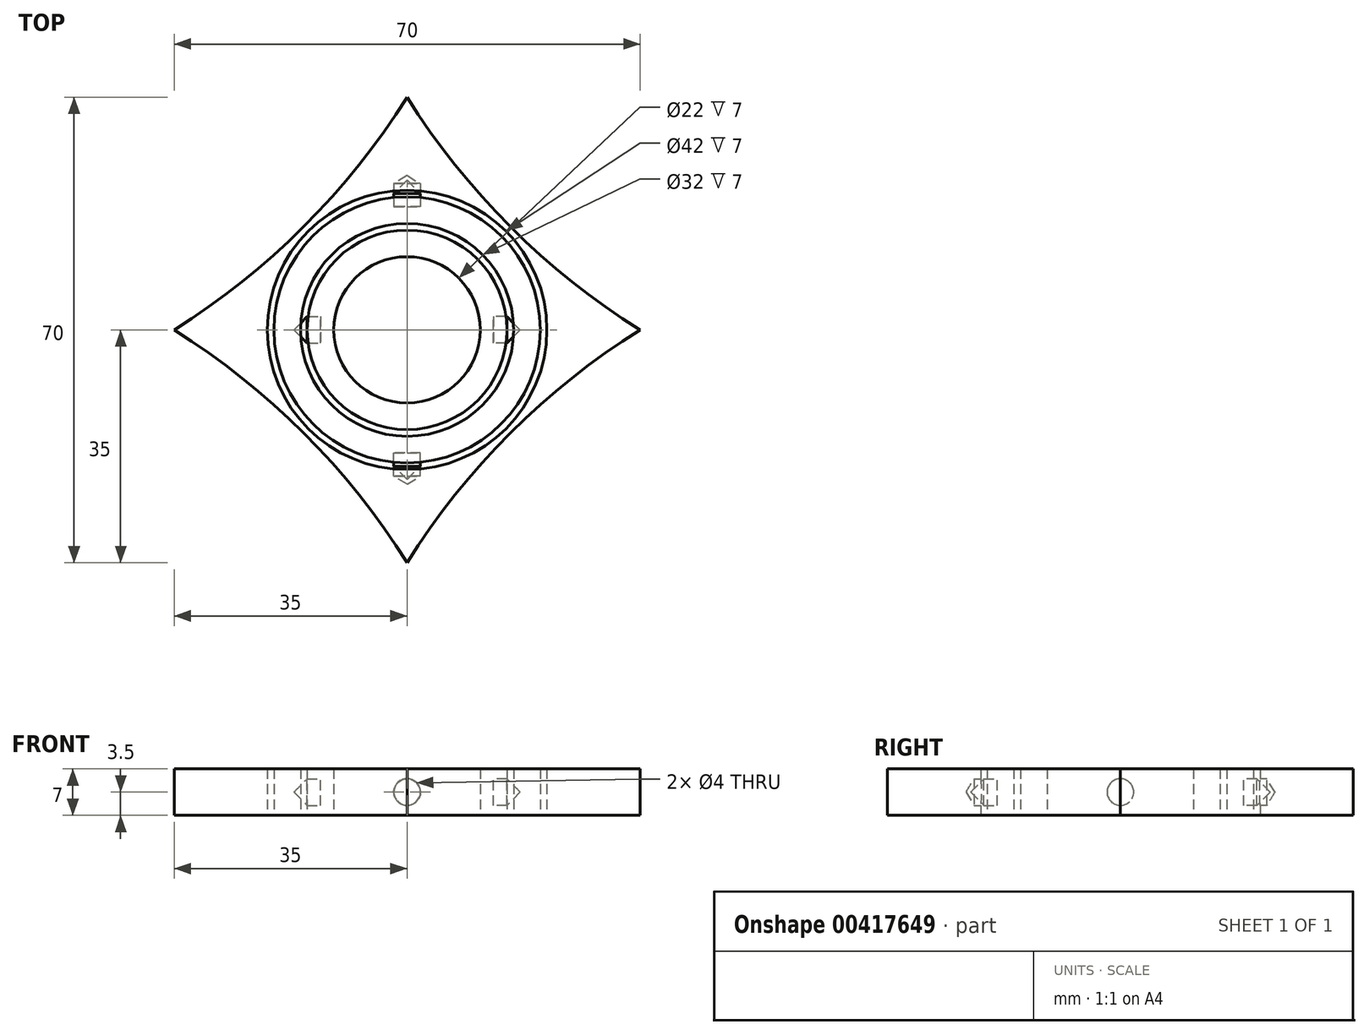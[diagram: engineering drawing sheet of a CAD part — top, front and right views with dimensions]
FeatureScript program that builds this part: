
annotation { "Feature Type Name" : "Feature", "Feature Type Description" : "" }
export const myFeature = defineFeature(function(context is Context, id is Id, definition is map)
    precondition{}
    {
        {
            var Q0;
            Q0=qCreatedBy(makeId("Top.planeOp"),FACE);
            var sketch = newSketch(context, id + "F0", { "sketchPlane" : qUnion([Q0])});
            skCircle(sketch, "E0", {"center": v(0, 0) * mm, "radius": 11 * mm});
            skCircle(sketch, "E1.0", {"center": v(0, 0) * mm, "radius": 15 * mm});
            skSolve(sketch);
        }
        {
            var Q0;
            Q0=makeQuery(id+"F0.imprint","IMPRINT",FACE,{"disambiguationData":[TD([[makeQuery(id+"F0.imprint","IMPRINT",EDGE,{"derivedFrom":sQuery(id+"F0.wireOp",EDGE,"E0")}),-1.0]])]});
            extrude(context, id + "F1", {"entities" : qUnion([Q0]), "endBound" : BoundingType.SYMMETRIC, "depth" : 7 * mm});
        }
        {
            var Q0;
            Q0=qCreatedBy(makeId("Right.planeOp"),FACE);
            cPlane(context, id + "F2", {"entities" : qUnion([Q0]), "cplaneType" : CPlaneType.OFFSET, "offset" : 13 * mm, "width" : 150 * mm, "height" : 150 * mm});
        }
        {
            var Q0;
            Q0=qCreatedBy(id+"F2.planeOp",FACE);
            var sketch = newSketch(context, id + "F3", { "sketchPlane" : qUnion([Q0])});
            skCircle(sketch, "E2", {"center": v(0, 0) * mm, "radius": 2 * mm});
            skSolve(sketch);
        }
        {
            var Q0;
            Q0=qCreatedBy(makeId("Right.planeOp"),FACE);
            cPlane(context, id + "F4", {"entities" : qUnion([Q0]), "cplaneType" : CPlaneType.OFFSET, "offset" : 15.82 * mm, "width" : 150 * mm, "height" : 150 * mm});
        }
        {
            var Q0;
            Q0=qCreatedBy(makeId("Top.planeOp"),FACE);
            var sketch = newSketch(context, id + "F5", { "sketchPlane" : qUnion([Q0])});
            skCircle(sketch, "E3", {"center": v(0, 0) * mm, "radius": 16 * mm});
            skCircle(sketch, "E4.0", {"center": v(0, 0) * mm, "radius": 20 * mm});
            skSolve(sketch);
        }
        {
            var Q0;
            Q0=makeQuery(id+"F5.imprint","IMPRINT",FACE,{"disambiguationData":[TD([[makeQuery(id+"F5.imprint","IMPRINT",EDGE,{"derivedFrom":sQuery(id+"F5.wireOp",EDGE,"E3")}),-1.0]])]});
            extrude(context, id + "F6", {"entities" : qUnion([Q0]), "endBound" : BoundingType.SYMMETRIC, "depth" : 7 * mm});
        }
        {
            var Q0;
            Q0=qSketchRegion(id+"F3",true);
            extrude(context, id + "F7", {"entities" : qUnion([Q0]), "depth" : 4 * mm});
        }
        {
            var Q0;
            Q0=makeQuery(id+"F7.opExtrude","CAP_FACE",FACE,{"disambiguationData":[OSD([sQuery(id+"F3.wireOp",EDGE,"E2")])],"isStart":false});
            chamfer(context, id + "F8", {"entities" : qUnion([Q0]), "width" : 2 * mm, "tangentPropagation" : true});
        }
        {
            var Q0;
            Q0=makeQuery(id+"F7.opExtrude","SWEPT_BODY",BODY,{"disambiguationData":[OSD([sQuery(id+"F3.wireOp",EDGE,"E2")])]});
            var Q1;
            Q1=qCreatedBy(makeId("Right.planeOp"),FACE);
            mirror(context, id + "F9", {"entities" : qUnion([Q0]), "mirrorPlane" : qUnion([Q1])});
        }
        {
            var Q0;
            Q0=qCreatedBy(makeId("Top.planeOp"),FACE);
            var sketch = newSketch(context, id + "F10", { "sketchPlane" : qUnion([Q0])});
            skCircle(sketch, "E5.0", {"center": v(0, 0) * mm, "radius": 21 * mm});
            skPoint(sketch, "E6", {"position": v(0, 25) * mm});
            skPoint(sketch, "E7", {"position": v(0, -25) * mm});
            skPoint(sketch, "E8", {"position": v(-25, 0) * mm});
            skPoint(sketch, "E9", {"position": v(25, 0) * mm});
            skLineSegment(sketch, "E10", {"start": v(0, 25) * mm, "end": v(0, 35) * mm});
            skLineSegment(sketch, "E11.1.0", {"start": v(-25, 0) * mm, "end": v(-35, 0) * mm});
            skLineSegment(sketch, "E11.2.0", {"start": v(0, -25) * mm, "end": v(0, -35) * mm});
            skLineSegment(sketch, "E11.3.0", {"start": v(25, 0) * mm, "end": v(35, 0) * mm});
            skArc(sketch, "E12", {"start": v(-35, 0) * mm, "mid": v(-15.52, 15.52) * mm, "end": v(0, 35) * mm});
            skArc(sketch, "E13.1.0", {"start": v(0, -35) * mm, "mid": v(-15.52, -15.52) * mm, "end": v(-35, 0) * mm});
            skArc(sketch, "E13.2.0", {"start": v(35, 0) * mm, "mid": v(15.52, -15.52) * mm, "end": v(0, -35) * mm});
            skArc(sketch, "E13.3.0", {"start": v(0, 35) * mm, "mid": v(15.52, 15.52) * mm, "end": v(35, 0) * mm});
            skSolve(sketch);
        }
        {
            var Q0;
            Q0=makeQuery(id+"F10.imprint","IMPRINT",FACE,{"disambiguationData":[TD([[makeQuery(id+"F10.imprint","IMPRINT",EDGE,{"derivedFrom":sQuery(id+"F10.wireOp",EDGE,"E5.0")}),-1.0]])]});
            extrude(context, id + "F11", {"entities" : qUnion([Q0]), "endBound" : BoundingType.SYMMETRIC, "depth" : 7 * mm});
        }
        {
            var Q0;
            Q0=qCreatedBy(makeId("Front.planeOp"),FACE);
            cPlane(context, id + "F12", {"entities" : qUnion([Q0]), "cplaneType" : CPlaneType.OFFSET, "offset" : 18.5 * mm, "width" : 150 * mm, "height" : 150 * mm});
        }
        {
            var Q0;
            Q0=qCreatedBy(id+"F12.planeOp",FACE);
            var sketch = newSketch(context, id + "F13", { "sketchPlane" : qUnion([Q0])});
            skCircle(sketch, "E14", {"center": v(0, 0) * mm, "radius": 2 * mm});
            skSolve(sketch);
        }
        {
            var Q0;
            Q0=qCreatedBy(makeId("Right.planeOp"),FACE);
            cPlane(context, id + "F14", {"entities" : qUnion([Q0]), "cplaneType" : CPlaneType.OFFSET, "offset" : 15.78 * mm, "oppositeDirection" : true, "width" : 150 * mm, "height" : 150 * mm});
        }
        {
            var Q0;
            Q0=qSketchRegion(id+"F13",true);
            extrude(context, id + "F15", {"entities" : qUnion([Q0]), "depth" : 4 * mm});
        }
        {
            var Q0;
            Q0=makeQuery(id+"F15.opExtrude","CAP_FACE",FACE,{"disambiguationData":[OSD([sQuery(id+"F13.wireOp",EDGE,"E14")])],"isStart":false});
            chamfer(context, id + "F16", {"entities" : qUnion([Q0]), "width" : 2 * mm, "tangentPropagation" : true});
        }
        {
            var Q0;
            Q0=qCreatedBy(makeId("Front.planeOp"),FACE);
            cPlane(context, id + "F17", {"entities" : qUnion([Q0]), "cplaneType" : CPlaneType.OFFSET, "offset" : 20.6 * mm, "width" : 150 * mm, "height" : 150 * mm});
        }
        {
            var Q0;
            Q0=qCreatedBy(id+"F17.planeOp",FACE);
            var sketch = newSketch(context, id + "F18", { "sketchPlane" : qUnion([Q0])});
            skCircle(sketch, "E15", {"center": v(0, 0) * mm, "radius": 2.03 * mm});
            skSolve(sketch);
        }
        {
            var Q0;
            Q0=sQuery(id+"F18.wireOp",VERTEX,"E15.center");
            var Q1;
            Q1=makeQuery(id+"F11.opExtrude","SWEPT_BODY",BODY,{"disambiguationData":[OSD([sQuery(id+"F10.wireOp",EDGE,"E5.0"),sQuery(id+"F10.wireOp",EDGE,"40ac9614-377f-489e-83ff-8fc2c02f8a50.0")])]});
            hole(context, id + "F19", {"style" : HoleStyle.SIMPLE, "endStyle" : HoleEndStyle.BLIND, "oppositeDirection" : true, "holeDiameter" : 4 * mm, "holeDepth" : 1 * mm, "isTappedThrough" : true, "tappedDepth" : 12 * mm, "tapClearance" : 3, "locations" : qUnion([Q0]), "scope" : qUnion([Q1])});
        }
        {
            var Q0;
            Q0=makeQuery(id+"F15.opExtrude","SWEPT_BODY",BODY,{"disambiguationData":[OSD([sQuery(id+"F13.wireOp",EDGE,"E14")])]});
            var Q1;
            Q1=qCreatedBy(makeId("Front.planeOp"),FACE);
            mirror(context, id + "F20", {"entities" : qUnion([Q0]), "mirrorPlane" : qUnion([Q1])});
        }
        {
            var Q0;
            Q0=qCreatedBy(makeId("Front.planeOp"),FACE);
            cPlane(context, id + "F21", {"entities" : qUnion([Q0]), "cplaneType" : CPlaneType.OFFSET, "offset" : 20.72 * mm, "oppositeDirection" : true, "width" : 150 * mm, "height" : 150 * mm});
        }
        {
            var Q0;
            Q0=qCreatedBy(id+"F21.planeOp",FACE);
            var sketch = newSketch(context, id + "F22", { "sketchPlane" : qUnion([Q0])});
            skCircle(sketch, "E16", {"center": v(0, 0) * mm, "radius": 2 * mm});
            skSolve(sketch);
        }
        {
            var Q0;
            Q0=sQuery(id+"F22.wireOp",VERTEX,"E16.center");
            var Q1;
            Q1=makeQuery(id+"F11.opExtrude","SWEPT_BODY",BODY,{"disambiguationData":[OSD([sQuery(id+"F10.wireOp",EDGE,"E5.0"),sQuery(id+"F10.wireOp",EDGE,"40ac9614-377f-489e-83ff-8fc2c02f8a50.0")])]});
            hole(context, id + "F23", {"style" : HoleStyle.SIMPLE, "endStyle" : HoleEndStyle.BLIND, "holeDiameter" : 4 * mm, "holeDepth" : 1 * mm, "isTappedThrough" : true, "tappedDepth" : 12 * mm, "tapClearance" : 3, "locations" : qUnion([Q0]), "scope" : qUnion([Q1])});
        }
    });
